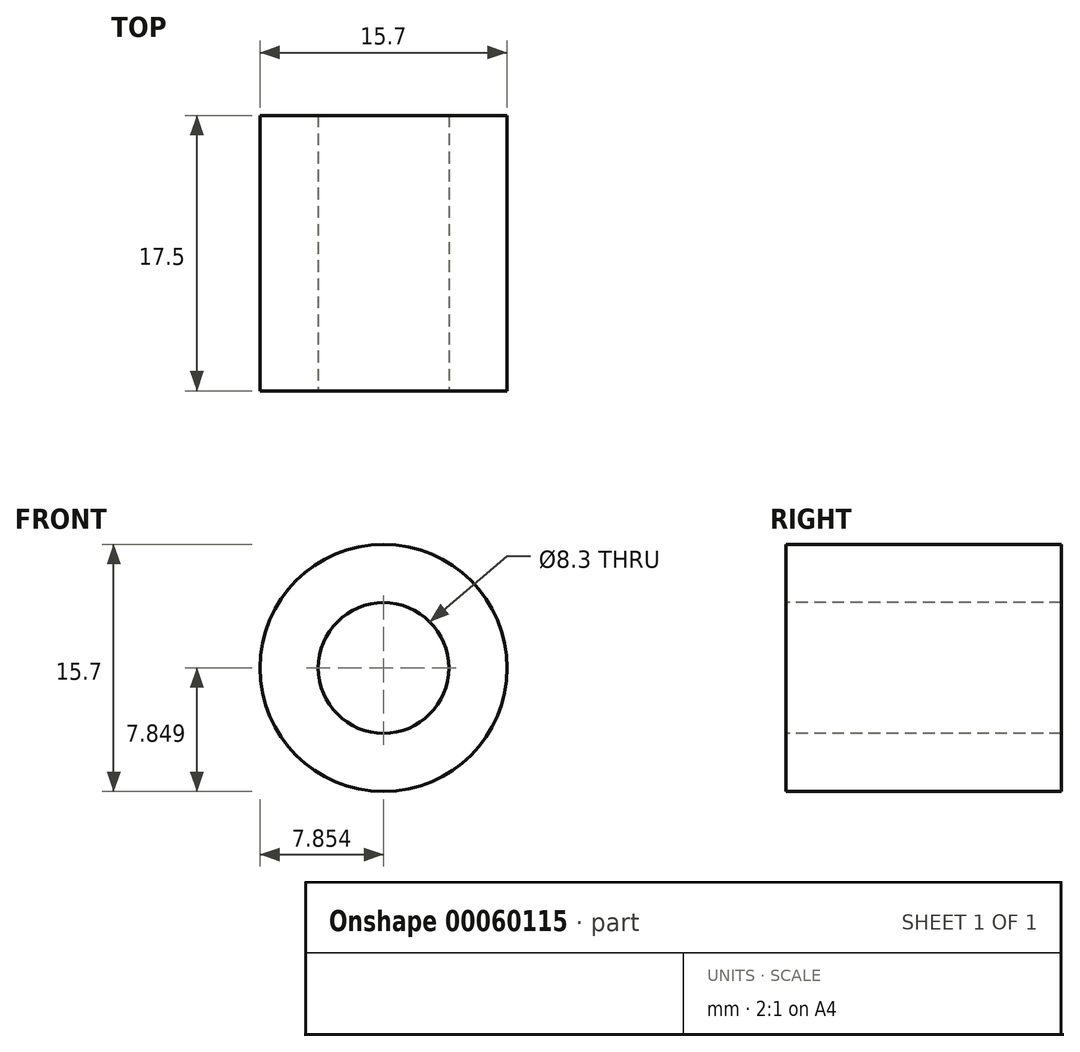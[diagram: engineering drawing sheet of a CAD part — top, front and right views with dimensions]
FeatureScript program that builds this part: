
annotation { "Feature Type Name" : "Feature", "Feature Type Description" : "" }
export const myFeature = defineFeature(function(context is Context, id is Id, definition is map)
    precondition{}
    {
        {
            var Q0;
            Q0=qCreatedBy(makeId("Front.planeOp"),FACE);
            var sketch = newSketch(context, id + "F0", { "sketchPlane" : qUnion([Q0])});
            skCircle(sketch, "E0", {"center": v(-40.78, 37.52) * mm, "radius": 7.85 * mm});
            skCircle(sketch, "E1", {"center": v(-40.78, 37.52) * mm, "radius": 4.15 * mm});
            skSolve(sketch);
        }
        {
            var Q0;
            Q0=makeQuery(id+"F0.imprint","IMPRINT",FACE,{"disambiguationData":[TD([[makeQuery(id+"F0.imprint","IMPRINT",EDGE,{"derivedFrom":sQuery(id+"F0.wireOp",EDGE,"E0")}),1.0]])]});
            extrude(context, id + "F1", {"entities" : qUnion([Q0]), "oppositeDirection" : true, "depth" : 17.5 * mm});
        }
    });
